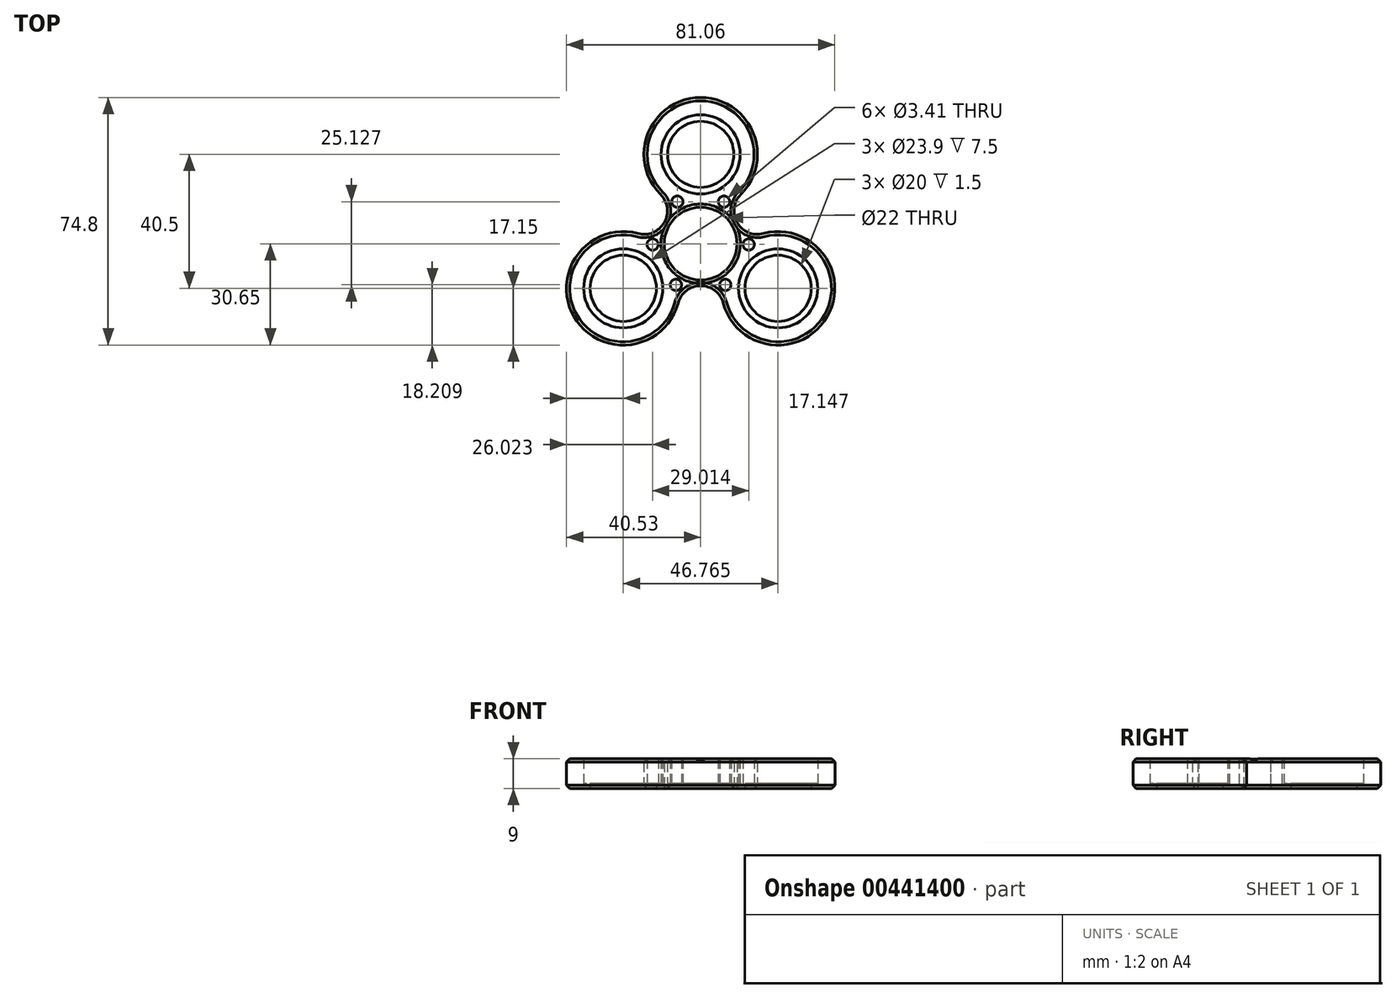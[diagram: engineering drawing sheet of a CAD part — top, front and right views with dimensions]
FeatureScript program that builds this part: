
annotation { "Feature Type Name" : "Feature", "Feature Type Description" : "" }
export const myFeature = defineFeature(function(context is Context, id is Id, definition is map)
    precondition{}
    {
        {
            var Q0;
            Q0=qCreatedBy(makeId("Top.planeOp"),FACE);
            var sketch = newSketch(context, id + "F0", { "sketchPlane" : qUnion([Q0])});
            skCircle(sketch, "E0", {"center": v(0, 0) * mm, "radius": 11 * mm});
            skCircle(sketch, "E1", {"center": v(0, 27) * mm, "radius": 11.95 * mm});
            skPoint(sketch, "E2.center", {"position": v(0, -0.02) * mm});
            skArc(sketch, "E3.0", {"start": v(12.13, 14.87) * mm, "mid": v(0, 44.15) * mm, "end": v(-12.13, 14.87) * mm});
            skCircle(sketch, "E4.1.0", {"center": v(-23.38, -13.5) * mm, "radius": 11.95 * mm});
            skArc(sketch, "E4.1.1", {"start": v(-18.94, 3.07) * mm, "mid": v(-38.24, -22.07) * mm, "end": v(-6.82, -17.94) * mm});
            skCircle(sketch, "E4.2.0", {"center": v(23.38, -13.5) * mm, "radius": 11.95 * mm});
            skArc(sketch, "E4.2.1", {"start": v(6.82, -17.94) * mm, "mid": v(38.24, -22.08) * mm, "end": v(18.94, 3.07) * mm});
            skArc(sketch, "E5", {"start": v(-12.13, 14.87) * mm, "mid": v(-11, 6.35) * mm, "end": v(-18.94, 3.07) * mm});
            skArc(sketch, "E6", {"start": v(-6.82, -17.94) * mm, "mid": v(0, -12.7) * mm, "end": v(6.82, -17.94) * mm});
            skArc(sketch, "E7", {"start": v(18.94, 3.07) * mm, "mid": v(11, 6.35) * mm, "end": v(12.13, 14.87) * mm});
            skPoint(sketch, "E8", {"position": v(-7.04, 12.69) * mm});
            skCircle(sketch, "E9", {"center": v(-7.04, 12.69) * mm, "radius": 1.7 * mm});
            skCircle(sketch, "E10.MirrorC", {"center": v(7.04, 12.69) * mm, "radius": 1.7 * mm});
            skCircle(sketch, "E11.1.0", {"center": v(-7.47, -12.44) * mm, "radius": 1.7 * mm});
            skCircle(sketch, "E11.1.1", {"center": v(-14.5, -0.25) * mm, "radius": 1.7 * mm});
            skCircle(sketch, "E11.2.0", {"center": v(14.5, -0.25) * mm, "radius": 1.7 * mm});
            skCircle(sketch, "E11.2.1", {"center": v(7.47, -12.44) * mm, "radius": 1.7 * mm});
            skCircle(sketch, "E12", {"center": v(0, 27) * mm, "radius": 10 * mm});
            skCircle(sketch, "E13", {"center": v(-23.38, -13.5) * mm, "radius": 10 * mm});
            skCircle(sketch, "E14", {"center": v(23.38, -13.5) * mm, "radius": 10 * mm});
            skSolve(sketch);
        }
        {
            var Q0;
            Q0=makeQuery(id+"F0.imprint","IMPRINT",FACE,{"disambiguationData":[TD([[makeQuery(id+"F0.imprint","IMPRINT",EDGE,{"derivedFrom":sQuery(id+"F0.wireOp",EDGE,"E0")}),-1.0]])]});
            extrude(context, id + "F1", {"entities" : qUnion([Q0]), "depth" : 9 * mm});
        }
        {
            var Q0;
            Q0=makeQuery(id+"F1.opExtrude","CAP_EDGE",EDGE,{"disambiguationData":[OSD([sQuery(id+"F0.wireOp",EDGE,"E4.1.1")])],"isStart":false});
            var Q1;
            Q1=makeQuery(id+"F1.opExtrude","CAP_EDGE",EDGE,{"disambiguationData":[OSD([sQuery(id+"F0.wireOp",EDGE,"E6")])],"isStart":false});
            var Q2;
            Q2=makeQuery(id+"F1.opExtrude","CAP_EDGE",EDGE,{"disambiguationData":[OSD([sQuery(id+"F0.wireOp",EDGE,"E4.2.1")])],"isStart":false});
            var Q3;
            Q3=makeQuery(id+"F1.opExtrude","CAP_EDGE",EDGE,{"disambiguationData":[OSD([sQuery(id+"F0.wireOp",EDGE,"E4.2.1")])],"isStart":true});
            var Q4;
            Q4=makeQuery(id+"F1.opExtrude","CAP_EDGE",EDGE,{"disambiguationData":[OSD([sQuery(id+"F0.wireOp",EDGE,"E6")])],"isStart":true});
            var Q5;
            Q5=makeQuery(id+"F1.opExtrude","CAP_EDGE",EDGE,{"disambiguationData":[OSD([sQuery(id+"F0.wireOp",EDGE,"E4.1.1")])],"isStart":true});
            var Q6;
            Q6=makeQuery(id+"F1.opExtrude","CAP_EDGE",EDGE,{"disambiguationData":[OSD([sQuery(id+"F0.wireOp",EDGE,"E5")])],"isStart":false});
            var Q7;
            Q7=makeQuery(id+"F1.opExtrude","CAP_EDGE",EDGE,{"disambiguationData":[OSD([sQuery(id+"F0.wireOp",EDGE,"E5")])],"isStart":true});
            var Q8;
            Q8=makeQuery(id+"F1.opExtrude","CAP_EDGE",EDGE,{"disambiguationData":[OSD([sQuery(id+"F0.wireOp",EDGE,"E3.0")])],"isStart":true});
            var Q9;
            Q9=makeQuery(id+"F1.opExtrude","CAP_EDGE",EDGE,{"disambiguationData":[OSD([sQuery(id+"F0.wireOp",EDGE,"E3.0")])],"isStart":false});
            var Q10;
            Q10=makeQuery(id+"F1.opExtrude","CAP_EDGE",EDGE,{"disambiguationData":[OSD([sQuery(id+"F0.wireOp",EDGE,"E7")])],"isStart":false});
            var Q11;
            Q11=makeQuery(id+"F1.opExtrude","CAP_EDGE",EDGE,{"disambiguationData":[OSD([sQuery(id+"F0.wireOp",EDGE,"E7")])],"isStart":true});
            chamfer(context, id + "F2", {"entities" : qUnion([Q0, Q1, Q2, Q3, Q4, Q5, Q6, Q7, Q8, Q9, Q10, Q11]), "width" : 1 * mm, "tangentPropagation" : true});
        }
        {
            var Q0;
            Q0=makeQuery(id+"F0.imprint","IMPRINT",FACE,{"disambiguationData":[TD([[makeQuery(id+"F0.imprint","IMPRINT",EDGE,{"derivedFrom":sQuery(id+"F0.wireOp",EDGE,"E1")}),1.0]])]});
            var Q1;
            Q1=makeQuery(id+"F0.imprint","IMPRINT",FACE,{"disambiguationData":[TD([[makeQuery(id+"F0.imprint","IMPRINT",EDGE,{"derivedFrom":sQuery(id+"F0.wireOp",EDGE,"E4.1.0")}),1.0]])]});
            var Q2;
            Q2=makeQuery(id+"F0.imprint","IMPRINT",FACE,{"disambiguationData":[TD([[makeQuery(id+"F0.imprint","IMPRINT",EDGE,{"derivedFrom":sQuery(id+"F0.wireOp",EDGE,"E4.2.0")}),1.0]])]});
            extrude(context, id + "F3", {"entities" : qUnion([Q0, Q1, Q2]), "operationType" : NewBodyOperationType.ADD, "depth" : 1.5 * mm});
        }
        {
            var Q0;
            Q0=makeQuery(id+"F1.opExtrude","CAP_EDGE",EDGE,{"disambiguationData":[OSD([sQuery(id+"F0.wireOp",EDGE,"E0")])],"isStart":false});
            chamfer(context, id + "F4", {"entities" : qUnion([Q0]), "width" : 1 * mm, "tangentPropagation" : true});
        }
    });
